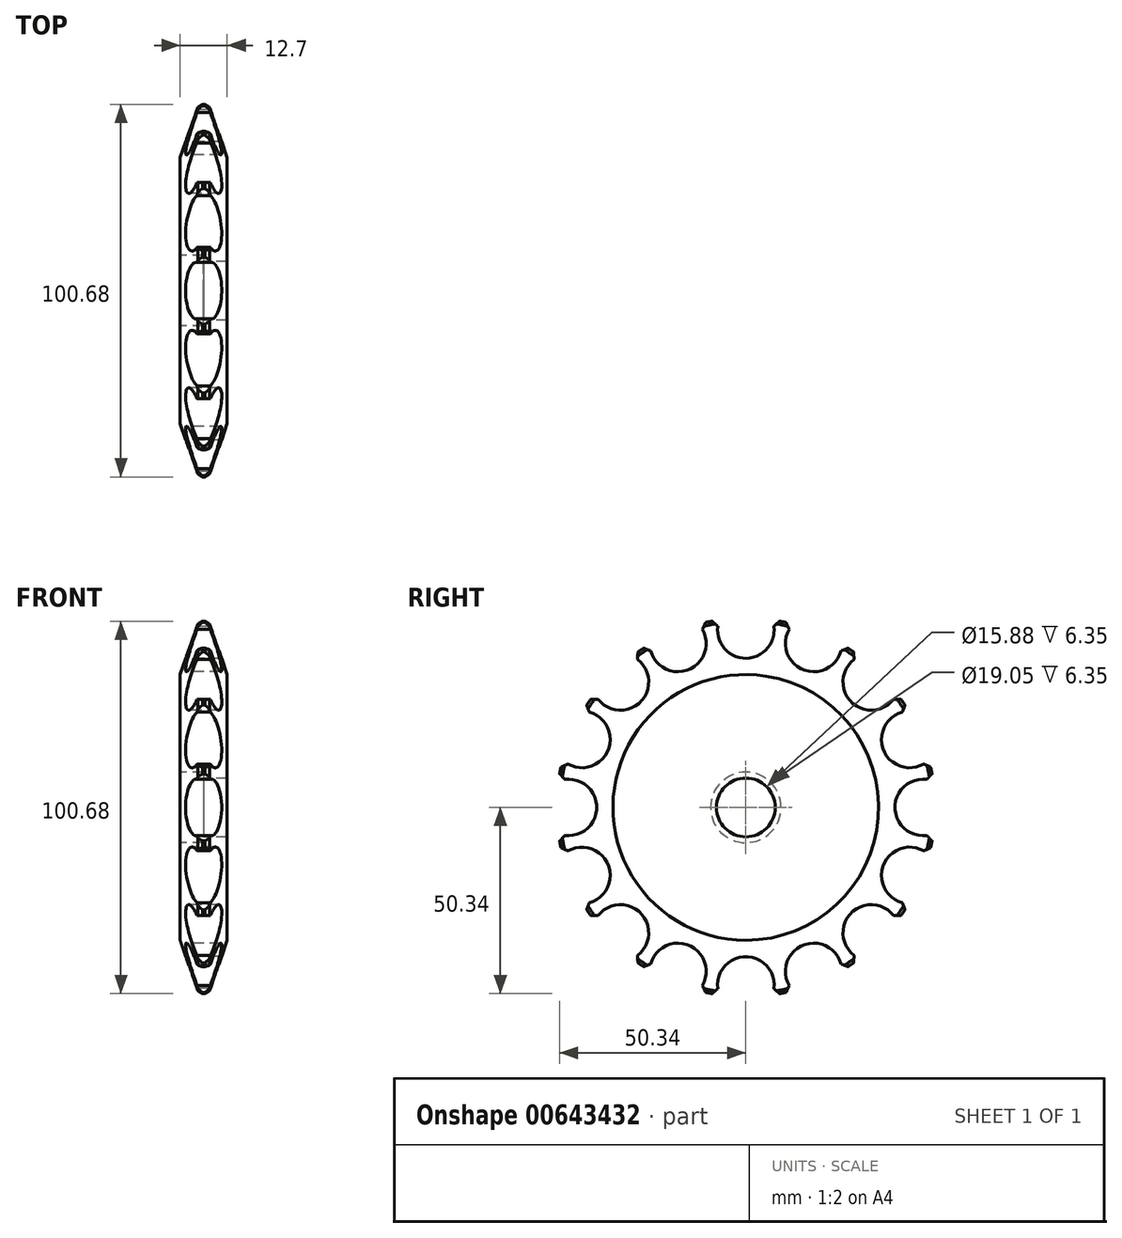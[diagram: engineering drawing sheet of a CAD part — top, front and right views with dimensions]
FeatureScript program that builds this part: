
annotation { "Feature Type Name" : "Feature", "Feature Type Description" : "" }
export const myFeature = defineFeature(function(context is Context, id is Id, definition is map)
    precondition{}
    {
        {
            var Q0;
            Q0=qCreatedBy(makeId("Right.planeOp"),FACE);
            var sketch = newSketch(context, id + "F0", { "sketchPlane" : qUnion([Q0])});
            skCircle(sketch, "E0", {"center": v(0, 0) * mm, "radius": 51.15 * mm});
            skSolve(sketch);
        }
        {
            var Q0;
            Q0=makeQuery(id+"F0.imprint","IMPRINT",FACE,{"disambiguationData":[TD([[makeQuery(id+"F0.imprint","IMPRINT",EDGE,{"derivedFrom":sQuery(id+"F0.wireOp",EDGE,"E0")}),1.0]])]});
            extrude(context, id + "F1", {"entities" : qUnion([Q0]), "depth" : 12.7 * mm, "offsetDistance" : 25.4 * mm});
        }
        {
            var Q0;
            Q0=makeQuery(id+"F1.opExtrude","CAP_EDGE",EDGE,{"disambiguationData":[OSD([sQuery(id+"F0.wireOp",EDGE,"E0")])],"isStart":true});
            var Q1;
            Q1=makeQuery(id+"F1.opExtrude","CAP_EDGE",EDGE,{"disambiguationData":[OSD([sQuery(id+"F0.wireOp",EDGE,"E0")])],"isStart":false});
            chamfer(context, id + "F2", {"entities" : qUnion([Q0, Q1]), "chamferType" : ChamferType.TWO_OFFSETS, "width1" : 5.08 * mm, "oppositeDirection" : false, "width2" : 15.24 * mm, "tangentPropagation" : true});
        }
        {
            var Q0;
            Q0=qCreatedBy(makeId("Right.planeOp"),FACE);
            var sketch = newSketch(context, id + "F3", { "sketchPlane" : qUnion([Q0])});
            skLineSegment(sketch, "E1", {"start": v(0, 0) * mm, "end": v(0, 66.32) * mm, "construction": true});
            skPoint(sketch, "E2", {"position": v(0, 51.15) * mm});
            skPoint(sketch, "E3", {"position": v(0, 35.91) * mm});
            skCircle(sketch, "E4", {"center": v(0, 47.96) * mm, "radius": 7.64 * mm});
            skCircle(sketch, "E5.1.0", {"center": v(-18.35, 44.3) * mm, "radius": 7.64 * mm});
            skCircle(sketch, "E5.2.0", {"center": v(-33.91, 33.91) * mm, "radius": 7.64 * mm});
            skCircle(sketch, "E5.3.0", {"center": v(-44.3, 18.35) * mm, "radius": 7.64 * mm});
            skCircle(sketch, "E5.4.0", {"center": v(-47.96, 0) * mm, "radius": 7.64 * mm});
            skCircle(sketch, "E5.5.0", {"center": v(-44.3, -18.35) * mm, "radius": 7.64 * mm});
            skCircle(sketch, "E5.6.0", {"center": v(-33.91, -33.91) * mm, "radius": 7.64 * mm});
            skCircle(sketch, "E5.7.0", {"center": v(-18.35, -44.3) * mm, "radius": 7.64 * mm});
            skCircle(sketch, "E5.8.0", {"center": v(0, -47.96) * mm, "radius": 7.64 * mm});
            skCircle(sketch, "E5.9.0", {"center": v(18.35, -44.3) * mm, "radius": 7.64 * mm});
            skCircle(sketch, "E5.10.0", {"center": v(33.91, -33.91) * mm, "radius": 7.64 * mm});
            skCircle(sketch, "E5.11.0", {"center": v(44.3, -18.35) * mm, "radius": 7.64 * mm});
            skCircle(sketch, "E5.12.0", {"center": v(47.96, 0) * mm, "radius": 7.64 * mm});
            skCircle(sketch, "E5.13.0", {"center": v(44.3, 18.35) * mm, "radius": 7.64 * mm});
            skCircle(sketch, "E5.14.0", {"center": v(33.91, 33.91) * mm, "radius": 7.64 * mm});
            skPoint(sketch, "E5.center", {"position": v(0, 0) * mm});
            skCircle(sketch, "E6.1.15.0", {"center": v(18.35, 44.3) * mm, "radius": 7.64 * mm});
            skSolve(sketch);
        }
        {
            var Q0;
            Q0 = qSketchRegion(id + "F3", true);
            extrude(context, id + "F4", {"entities" : qUnion([Q0]), "operationType" : NewBodyOperationType.REMOVE, "endBound" : BoundingType.THROUGH_ALL, "depth" : 25.4 * mm, "offsetDistance" : 25.4 * mm});
        }
        {
            var Q0;
            Q0=sQuery(id+"F0.wireOp",VERTEX,"E0.center");
            var Q1;
            Q1=makeQuery(id+"F1.opExtrude","SWEPT_BODY",BODY,{"disambiguationData":[OSD([sQuery(id+"F0.wireOp",EDGE,"E0")])]});
            hole(context, id + "F5", {"style" : HoleStyle.C_BORE, "endStyle" : HoleEndStyle.THROUGH, "oppositeDirection" : true, "holeDiameter" : 15.88 * mm, "cBoreDiameter" : 19.05 * mm, "cBoreDepth" : 6.35 * mm, "majorDiameter" : 6.35 * mm, "isTappedThrough" : true, "tappedDepth" : 12.7 * mm, "tapClearance" : 3, "locations" : qUnion([Q0]), "scope" : qUnion([Q1])});
        }
        {
            var Q0;
            {var subQ0=sQuery(id+"F0.wireOp",EDGE,"E0");var subQ1=makeQuery(id+"F1.opExtrude","SWEPT_FACE",FACE,{"disambiguationData":[OSD([subQ0])]});var subQ2=makeQuery(id+"F1.opExtrude","CAP_EDGE",EDGE,{"disambiguationData":[OSD([subQ0])],"isStart":false});Q0=makeQuery(id+"F4.boolean.opBoolean","SPLIT",EDGE,{"disambiguationData":[TD([subQ1,makeQuery(id+"F2.opChamfer","BLEND_FACE",FACE,{"disambiguationData":[OSD([subQ0]),TDD([subQ2])]}),makeQuery(id+"F4.opExtrude","SWEPT_FACE",FACE,{"disambiguationData":[OSD([sQuery(id+"F3.wireOp",EDGE,"E5.10.0")])]}),makeQuery(id+"F4.opExtrude","SWEPT_FACE",FACE,{"disambiguationData":[OSD([sQuery(id+"F3.wireOp",EDGE,"E5.11.0")])]})])],"derivedFrom":makeQuery(id+"F2.opChamfer","BLEND_EDGE",EDGE,{"blendedFrom":[subQ2,subQ1],"blendedInto":[subQ1]})});}
            var Q1;
            {var subQ0=sQuery(id+"F0.wireOp",EDGE,"E0");Q1=makeQuery(id+"F4.boolean.opBoolean","SPLIT",FACE,{"disambiguationData":[TD([makeQuery(id+"F2.opChamfer","BLEND_FACE",FACE,{"disambiguationData":[OSD([subQ0]),TDD([makeQuery(id+"F1.opExtrude","CAP_EDGE",EDGE,{"disambiguationData":[OSD([subQ0])],"isStart":true})])]}),makeQuery(id+"F2.opChamfer","BLEND_FACE",FACE,{"disambiguationData":[OSD([subQ0]),TDD([makeQuery(id+"F1.opExtrude","CAP_EDGE",EDGE,{"disambiguationData":[OSD([subQ0])],"isStart":false})])]}),makeQuery(id+"F4.opExtrude","SWEPT_FACE",FACE,{"disambiguationData":[OSD([sQuery(id+"F3.wireOp",EDGE,"E5.9.0")])]}),makeQuery(id+"F4.opExtrude","SWEPT_FACE",FACE,{"disambiguationData":[OSD([sQuery(id+"F3.wireOp",EDGE,"E5.10.0")])]})])],"derivedFrom":makeQuery(id+"F1.opExtrude","SWEPT_FACE",FACE,{"disambiguationData":[OSD([subQ0])]})});}
            var Q2;
            {var subQ0=sQuery(id+"F0.wireOp",EDGE,"E0");Q2=makeQuery(id+"F4.boolean.opBoolean","SPLIT",FACE,{"disambiguationData":[TD([makeQuery(id+"F2.opChamfer","BLEND_FACE",FACE,{"disambiguationData":[OSD([subQ0]),TDD([makeQuery(id+"F1.opExtrude","CAP_EDGE",EDGE,{"disambiguationData":[OSD([subQ0])],"isStart":true})])]}),makeQuery(id+"F2.opChamfer","BLEND_FACE",FACE,{"disambiguationData":[OSD([subQ0]),TDD([makeQuery(id+"F1.opExtrude","CAP_EDGE",EDGE,{"disambiguationData":[OSD([subQ0])],"isStart":false})])]}),makeQuery(id+"F4.opExtrude","SWEPT_FACE",FACE,{"disambiguationData":[OSD([sQuery(id+"F3.wireOp",EDGE,"E5.10.0")])]}),makeQuery(id+"F4.opExtrude","SWEPT_FACE",FACE,{"disambiguationData":[OSD([sQuery(id+"F3.wireOp",EDGE,"E5.11.0")])]})])],"derivedFrom":makeQuery(id+"F1.opExtrude","SWEPT_FACE",FACE,{"disambiguationData":[OSD([subQ0])]})});}
            var Q3;
            {var subQ0=sQuery(id+"F0.wireOp",EDGE,"E0");Q3=makeQuery(id+"F4.boolean.opBoolean","SPLIT",FACE,{"disambiguationData":[TD([makeQuery(id+"F2.opChamfer","BLEND_FACE",FACE,{"disambiguationData":[OSD([subQ0]),TDD([makeQuery(id+"F1.opExtrude","CAP_EDGE",EDGE,{"disambiguationData":[OSD([subQ0])],"isStart":true})])]}),makeQuery(id+"F2.opChamfer","BLEND_FACE",FACE,{"disambiguationData":[OSD([subQ0]),TDD([makeQuery(id+"F1.opExtrude","CAP_EDGE",EDGE,{"disambiguationData":[OSD([subQ0])],"isStart":false})])]}),makeQuery(id+"F4.opExtrude","SWEPT_FACE",FACE,{"disambiguationData":[OSD([sQuery(id+"F3.wireOp",EDGE,"E5.8.0")])]}),makeQuery(id+"F4.opExtrude","SWEPT_FACE",FACE,{"disambiguationData":[OSD([sQuery(id+"F3.wireOp",EDGE,"E5.9.0")])]})])],"derivedFrom":makeQuery(id+"F1.opExtrude","SWEPT_FACE",FACE,{"disambiguationData":[OSD([subQ0])]})});}
            var Q4;
            {var subQ0=sQuery(id+"F0.wireOp",EDGE,"E0");Q4=makeQuery(id+"F4.boolean.opBoolean","SPLIT",FACE,{"disambiguationData":[TD([makeQuery(id+"F2.opChamfer","BLEND_FACE",FACE,{"disambiguationData":[OSD([subQ0]),TDD([makeQuery(id+"F1.opExtrude","CAP_EDGE",EDGE,{"disambiguationData":[OSD([subQ0])],"isStart":true})])]}),makeQuery(id+"F2.opChamfer","BLEND_FACE",FACE,{"disambiguationData":[OSD([subQ0]),TDD([makeQuery(id+"F1.opExtrude","CAP_EDGE",EDGE,{"disambiguationData":[OSD([subQ0])],"isStart":false})])]}),makeQuery(id+"F4.opExtrude","SWEPT_FACE",FACE,{"disambiguationData":[OSD([sQuery(id+"F3.wireOp",EDGE,"E5.7.0")])]}),makeQuery(id+"F4.opExtrude","SWEPT_FACE",FACE,{"disambiguationData":[OSD([sQuery(id+"F3.wireOp",EDGE,"E5.8.0")])]})])],"derivedFrom":makeQuery(id+"F1.opExtrude","SWEPT_FACE",FACE,{"disambiguationData":[OSD([subQ0])]})});}
            var Q5;
            {var subQ0=sQuery(id+"F0.wireOp",EDGE,"E0");Q5=makeQuery(id+"F4.boolean.opBoolean","SPLIT",FACE,{"disambiguationData":[TD([makeQuery(id+"F2.opChamfer","BLEND_FACE",FACE,{"disambiguationData":[OSD([subQ0]),TDD([makeQuery(id+"F1.opExtrude","CAP_EDGE",EDGE,{"disambiguationData":[OSD([subQ0])],"isStart":true})])]}),makeQuery(id+"F2.opChamfer","BLEND_FACE",FACE,{"disambiguationData":[OSD([subQ0]),TDD([makeQuery(id+"F1.opExtrude","CAP_EDGE",EDGE,{"disambiguationData":[OSD([subQ0])],"isStart":false})])]}),makeQuery(id+"F4.opExtrude","SWEPT_FACE",FACE,{"disambiguationData":[OSD([sQuery(id+"F3.wireOp",EDGE,"E5.6.0")])]}),makeQuery(id+"F4.opExtrude","SWEPT_FACE",FACE,{"disambiguationData":[OSD([sQuery(id+"F3.wireOp",EDGE,"E5.7.0")])]})])],"derivedFrom":makeQuery(id+"F1.opExtrude","SWEPT_FACE",FACE,{"disambiguationData":[OSD([subQ0])]})});}
            var Q6;
            {var subQ0=sQuery(id+"F0.wireOp",EDGE,"E0");Q6=makeQuery(id+"F4.boolean.opBoolean","SPLIT",FACE,{"disambiguationData":[TD([makeQuery(id+"F2.opChamfer","BLEND_FACE",FACE,{"disambiguationData":[OSD([subQ0]),TDD([makeQuery(id+"F1.opExtrude","CAP_EDGE",EDGE,{"disambiguationData":[OSD([subQ0])],"isStart":true})])]}),makeQuery(id+"F2.opChamfer","BLEND_FACE",FACE,{"disambiguationData":[OSD([subQ0]),TDD([makeQuery(id+"F1.opExtrude","CAP_EDGE",EDGE,{"disambiguationData":[OSD([subQ0])],"isStart":false})])]}),makeQuery(id+"F4.opExtrude","SWEPT_FACE",FACE,{"disambiguationData":[OSD([sQuery(id+"F3.wireOp",EDGE,"E5.5.0")])]}),makeQuery(id+"F4.opExtrude","SWEPT_FACE",FACE,{"disambiguationData":[OSD([sQuery(id+"F3.wireOp",EDGE,"E5.6.0")])]})])],"derivedFrom":makeQuery(id+"F1.opExtrude","SWEPT_FACE",FACE,{"disambiguationData":[OSD([subQ0])]})});}
            var Q7;
            {var subQ0=sQuery(id+"F0.wireOp",EDGE,"E0");Q7=makeQuery(id+"F4.boolean.opBoolean","SPLIT",FACE,{"disambiguationData":[TD([makeQuery(id+"F2.opChamfer","BLEND_FACE",FACE,{"disambiguationData":[OSD([subQ0]),TDD([makeQuery(id+"F1.opExtrude","CAP_EDGE",EDGE,{"disambiguationData":[OSD([subQ0])],"isStart":true})])]}),makeQuery(id+"F2.opChamfer","BLEND_FACE",FACE,{"disambiguationData":[OSD([subQ0]),TDD([makeQuery(id+"F1.opExtrude","CAP_EDGE",EDGE,{"disambiguationData":[OSD([subQ0])],"isStart":false})])]}),makeQuery(id+"F4.opExtrude","SWEPT_FACE",FACE,{"disambiguationData":[OSD([sQuery(id+"F3.wireOp",EDGE,"E5.4.0")])]}),makeQuery(id+"F4.opExtrude","SWEPT_FACE",FACE,{"disambiguationData":[OSD([sQuery(id+"F3.wireOp",EDGE,"E5.5.0")])]})])],"derivedFrom":makeQuery(id+"F1.opExtrude","SWEPT_FACE",FACE,{"disambiguationData":[OSD([subQ0])]})});}
            var Q8;
            {var subQ0=sQuery(id+"F0.wireOp",EDGE,"E0");Q8=makeQuery(id+"F4.boolean.opBoolean","SPLIT",FACE,{"disambiguationData":[TD([makeQuery(id+"F2.opChamfer","BLEND_FACE",FACE,{"disambiguationData":[OSD([subQ0]),TDD([makeQuery(id+"F1.opExtrude","CAP_EDGE",EDGE,{"disambiguationData":[OSD([subQ0])],"isStart":true})])]}),makeQuery(id+"F2.opChamfer","BLEND_FACE",FACE,{"disambiguationData":[OSD([subQ0]),TDD([makeQuery(id+"F1.opExtrude","CAP_EDGE",EDGE,{"disambiguationData":[OSD([subQ0])],"isStart":false})])]}),makeQuery(id+"F4.opExtrude","SWEPT_FACE",FACE,{"disambiguationData":[OSD([sQuery(id+"F3.wireOp",EDGE,"E5.3.0")])]}),makeQuery(id+"F4.opExtrude","SWEPT_FACE",FACE,{"disambiguationData":[OSD([sQuery(id+"F3.wireOp",EDGE,"E5.4.0")])]})])],"derivedFrom":makeQuery(id+"F1.opExtrude","SWEPT_FACE",FACE,{"disambiguationData":[OSD([subQ0])]})});}
            var Q9;
            {var subQ0=sQuery(id+"F0.wireOp",EDGE,"E0");Q9=makeQuery(id+"F4.boolean.opBoolean","SPLIT",FACE,{"disambiguationData":[TD([makeQuery(id+"F2.opChamfer","BLEND_FACE",FACE,{"disambiguationData":[OSD([subQ0]),TDD([makeQuery(id+"F1.opExtrude","CAP_EDGE",EDGE,{"disambiguationData":[OSD([subQ0])],"isStart":true})])]}),makeQuery(id+"F2.opChamfer","BLEND_FACE",FACE,{"disambiguationData":[OSD([subQ0]),TDD([makeQuery(id+"F1.opExtrude","CAP_EDGE",EDGE,{"disambiguationData":[OSD([subQ0])],"isStart":false})])]}),makeQuery(id+"F4.opExtrude","SWEPT_FACE",FACE,{"disambiguationData":[OSD([sQuery(id+"F3.wireOp",EDGE,"E5.2.0")])]}),makeQuery(id+"F4.opExtrude","SWEPT_FACE",FACE,{"disambiguationData":[OSD([sQuery(id+"F3.wireOp",EDGE,"E5.3.0")])]})])],"derivedFrom":makeQuery(id+"F1.opExtrude","SWEPT_FACE",FACE,{"disambiguationData":[OSD([subQ0])]})});}
            var Q10;
            {var subQ0=sQuery(id+"F0.wireOp",EDGE,"E0");Q10=makeQuery(id+"F4.boolean.opBoolean","SPLIT",FACE,{"disambiguationData":[TD([makeQuery(id+"F2.opChamfer","BLEND_FACE",FACE,{"disambiguationData":[OSD([subQ0]),TDD([makeQuery(id+"F1.opExtrude","CAP_EDGE",EDGE,{"disambiguationData":[OSD([subQ0])],"isStart":true})])]}),makeQuery(id+"F2.opChamfer","BLEND_FACE",FACE,{"disambiguationData":[OSD([subQ0]),TDD([makeQuery(id+"F1.opExtrude","CAP_EDGE",EDGE,{"disambiguationData":[OSD([subQ0])],"isStart":false})])]}),makeQuery(id+"F4.opExtrude","SWEPT_FACE",FACE,{"disambiguationData":[OSD([sQuery(id+"F3.wireOp",EDGE,"E5.1.0")])]}),makeQuery(id+"F4.opExtrude","SWEPT_FACE",FACE,{"disambiguationData":[OSD([sQuery(id+"F3.wireOp",EDGE,"E5.2.0")])]})])],"derivedFrom":makeQuery(id+"F1.opExtrude","SWEPT_FACE",FACE,{"disambiguationData":[OSD([subQ0])]})});}
            var Q11;
            {var subQ0=sQuery(id+"F0.wireOp",EDGE,"E0");Q11=makeQuery(id+"F4.boolean.opBoolean","SPLIT",FACE,{"disambiguationData":[TD([makeQuery(id+"F2.opChamfer","BLEND_FACE",FACE,{"disambiguationData":[OSD([subQ0]),TDD([makeQuery(id+"F1.opExtrude","CAP_EDGE",EDGE,{"disambiguationData":[OSD([subQ0])],"isStart":true})])]}),makeQuery(id+"F2.opChamfer","BLEND_FACE",FACE,{"disambiguationData":[OSD([subQ0]),TDD([makeQuery(id+"F1.opExtrude","CAP_EDGE",EDGE,{"disambiguationData":[OSD([subQ0])],"isStart":false})])]}),makeQuery(id+"F4.opExtrude","SWEPT_FACE",FACE,{"disambiguationData":[OSD([sQuery(id+"F3.wireOp",EDGE,"E4")])]}),makeQuery(id+"F4.opExtrude","SWEPT_FACE",FACE,{"disambiguationData":[OSD([sQuery(id+"F3.wireOp",EDGE,"E5.1.0")])]})])],"derivedFrom":makeQuery(id+"F1.opExtrude","SWEPT_FACE",FACE,{"disambiguationData":[OSD([subQ0])]})});}
            var Q12;
            {var subQ0=sQuery(id+"F0.wireOp",EDGE,"E0");Q12=makeQuery(id+"F4.boolean.opBoolean","SPLIT",FACE,{"disambiguationData":[TD([makeQuery(id+"F2.opChamfer","BLEND_FACE",FACE,{"disambiguationData":[OSD([subQ0]),TDD([makeQuery(id+"F1.opExtrude","CAP_EDGE",EDGE,{"disambiguationData":[OSD([subQ0])],"isStart":true})])]}),makeQuery(id+"F2.opChamfer","BLEND_FACE",FACE,{"disambiguationData":[OSD([subQ0]),TDD([makeQuery(id+"F1.opExtrude","CAP_EDGE",EDGE,{"disambiguationData":[OSD([subQ0])],"isStart":false})])]}),makeQuery(id+"F4.opExtrude","SWEPT_FACE",FACE,{"disambiguationData":[OSD([sQuery(id+"F3.wireOp",EDGE,"E4")])]}),makeQuery(id+"F4.opExtrude","SWEPT_FACE",FACE,{"disambiguationData":[OSD([sQuery(id+"F3.wireOp",EDGE,"E5.14.0")])]})])],"derivedFrom":makeQuery(id+"F1.opExtrude","SWEPT_FACE",FACE,{"disambiguationData":[OSD([subQ0])]})});}
            var Q13;
            {var subQ0=sQuery(id+"F0.wireOp",EDGE,"E0");Q13=makeQuery(id+"F4.boolean.opBoolean","SPLIT",FACE,{"disambiguationData":[TD([makeQuery(id+"F2.opChamfer","BLEND_FACE",FACE,{"disambiguationData":[OSD([subQ0]),TDD([makeQuery(id+"F1.opExtrude","CAP_EDGE",EDGE,{"disambiguationData":[OSD([subQ0])],"isStart":true})])]}),makeQuery(id+"F2.opChamfer","BLEND_FACE",FACE,{"disambiguationData":[OSD([subQ0]),TDD([makeQuery(id+"F1.opExtrude","CAP_EDGE",EDGE,{"disambiguationData":[OSD([subQ0])],"isStart":false})])]}),makeQuery(id+"F4.opExtrude","SWEPT_FACE",FACE,{"disambiguationData":[OSD([sQuery(id+"F3.wireOp",EDGE,"E5.13.0")])]}),makeQuery(id+"F4.opExtrude","SWEPT_FACE",FACE,{"disambiguationData":[OSD([sQuery(id+"F3.wireOp",EDGE,"E5.14.0")])]})])],"derivedFrom":makeQuery(id+"F1.opExtrude","SWEPT_FACE",FACE,{"disambiguationData":[OSD([subQ0])]})});}
            var Q14;
            {var subQ0=sQuery(id+"F0.wireOp",EDGE,"E0");Q14=makeQuery(id+"F4.boolean.opBoolean","SPLIT",FACE,{"disambiguationData":[TD([makeQuery(id+"F2.opChamfer","BLEND_FACE",FACE,{"disambiguationData":[OSD([subQ0]),TDD([makeQuery(id+"F1.opExtrude","CAP_EDGE",EDGE,{"disambiguationData":[OSD([subQ0])],"isStart":true})])]}),makeQuery(id+"F2.opChamfer","BLEND_FACE",FACE,{"disambiguationData":[OSD([subQ0]),TDD([makeQuery(id+"F1.opExtrude","CAP_EDGE",EDGE,{"disambiguationData":[OSD([subQ0])],"isStart":false})])]}),makeQuery(id+"F4.opExtrude","SWEPT_FACE",FACE,{"disambiguationData":[OSD([sQuery(id+"F3.wireOp",EDGE,"E5.12.0")])]}),makeQuery(id+"F4.opExtrude","SWEPT_FACE",FACE,{"disambiguationData":[OSD([sQuery(id+"F3.wireOp",EDGE,"E5.13.0")])]})])],"derivedFrom":makeQuery(id+"F1.opExtrude","SWEPT_FACE",FACE,{"disambiguationData":[OSD([subQ0])]})});}
            var Q15;
            {var subQ0=sQuery(id+"F0.wireOp",EDGE,"E0");Q15=makeQuery(id+"F4.boolean.opBoolean","SPLIT",FACE,{"disambiguationData":[TD([makeQuery(id+"F2.opChamfer","BLEND_FACE",FACE,{"disambiguationData":[OSD([subQ0]),TDD([makeQuery(id+"F1.opExtrude","CAP_EDGE",EDGE,{"disambiguationData":[OSD([subQ0])],"isStart":true})])]}),makeQuery(id+"F2.opChamfer","BLEND_FACE",FACE,{"disambiguationData":[OSD([subQ0]),TDD([makeQuery(id+"F1.opExtrude","CAP_EDGE",EDGE,{"disambiguationData":[OSD([subQ0])],"isStart":false})])]}),makeQuery(id+"F4.opExtrude","SWEPT_FACE",FACE,{"disambiguationData":[OSD([sQuery(id+"F3.wireOp",EDGE,"E5.11.0")])]}),makeQuery(id+"F4.opExtrude","SWEPT_FACE",FACE,{"disambiguationData":[OSD([sQuery(id+"F3.wireOp",EDGE,"E5.12.0")])]})])],"derivedFrom":makeQuery(id+"F1.opExtrude","SWEPT_FACE",FACE,{"disambiguationData":[OSD([subQ0])]})});}
            chamfer(context, id + "F6", {"entities" : qUnion([Q0, Q1, Q2, Q3, Q4, Q5, Q6, Q7, Q8, Q9, Q10, Q11, Q12, Q13, Q14, Q15]), "width" : 1.27 * mm, "tangentPropagation" : true});
        }
    });
